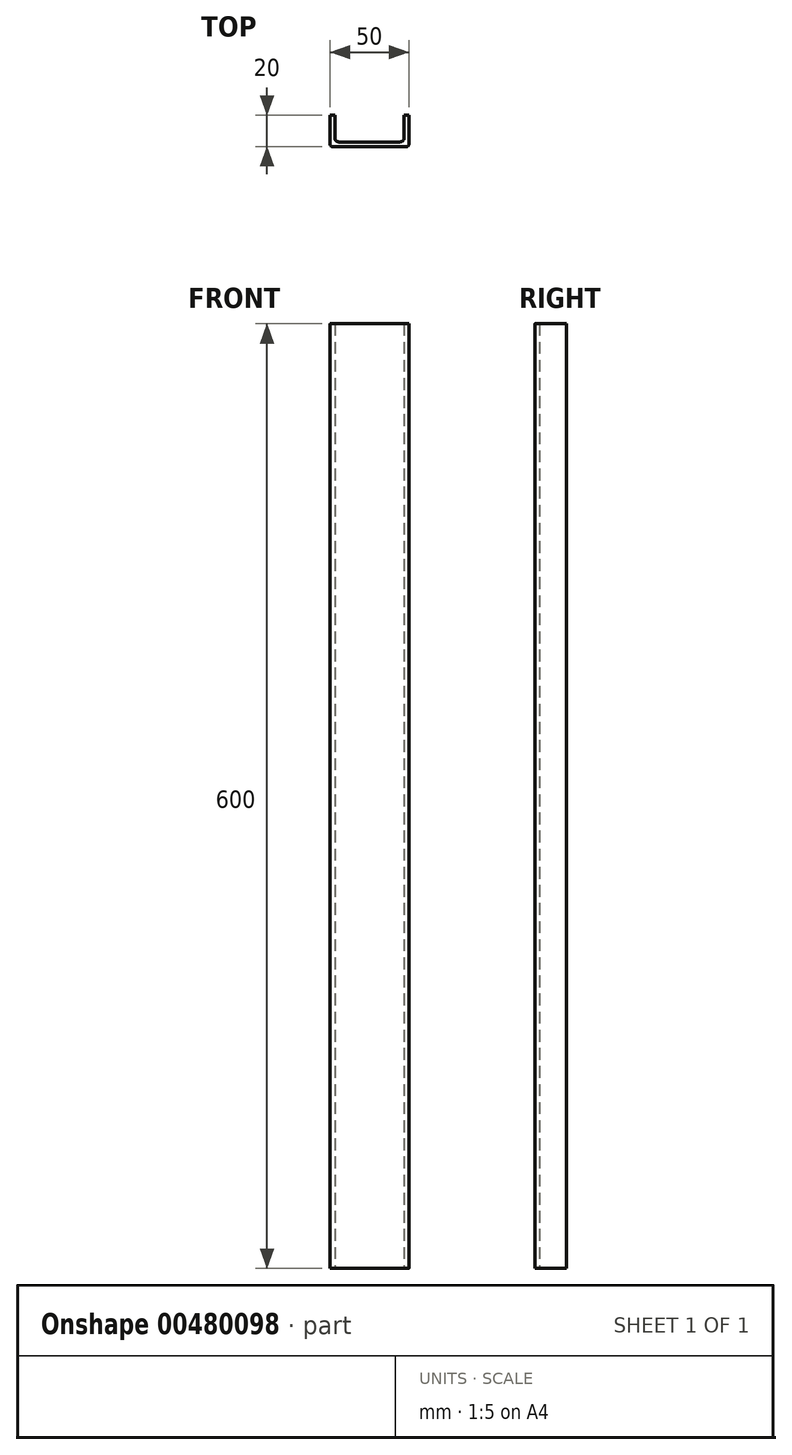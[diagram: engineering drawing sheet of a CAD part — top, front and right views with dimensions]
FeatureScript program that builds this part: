
annotation { "Feature Type Name" : "Feature", "Feature Type Description" : "" }
export const myFeature = defineFeature(function(context is Context, id is Id, definition is map)
    precondition{}
    {
        {
            var Q0;
            Q0=qCreatedBy(makeId("Top.planeOp"),FACE);
            var sketch = newSketch(context, id + "F0", { "sketchPlane" : qUnion([Q0])});
            skArc(sketch, "E0.0.endCap", {"start": v(0, -1.5) * mm, "mid": v(-1.06, -1.06) * mm, "end": v(-1.5, 0) * mm});
            skLineSegment(sketch, "E0.0.left", {"start": v(1.5, 18.5) * mm, "end": v(1.5, 4) * mm});
            skLineSegment(sketch, "E0.0.right", {"start": v(-1.5, 18.5) * mm, "end": v(-1.5, 0) * mm});
            skArc(sketch, "E0.1.startCap", {"start": v(0, -1.5) * mm, "mid": v(-1.06, -1.06) * mm, "end": v(-1.5, 0) * mm});
            skArc(sketch, "E0.1.endCap", {"start": v(48.5, 0) * mm, "mid": v(48.06, -1.06) * mm, "end": v(47, -1.5) * mm});
            skLineSegment(sketch, "E0.1.left", {"start": v(4, 1.5) * mm, "end": v(43, 1.5) * mm});
            skLineSegment(sketch, "E0.1.right", {"start": v(0, -1.5) * mm, "end": v(47, -1.5) * mm});
            skArc(sketch, "E0.2.startCap", {"start": v(48.5, 0) * mm, "mid": v(48.06, -1.06) * mm, "end": v(47, -1.5) * mm});
            skLineSegment(sketch, "E0.2.left", {"start": v(45.5, 4) * mm, "end": v(45.5, 18.5) * mm});
            skLineSegment(sketch, "E0.2.right", {"start": v(48.5, 0) * mm, "end": v(48.5, 18.5) * mm});
            skLineSegment(sketch, "E1", {"start": v(-1.5, 18.5) * mm, "end": v(1.5, 18.5) * mm});
            skLineSegment(sketch, "E2", {"start": v(45.5, 18.5) * mm, "end": v(48.5, 18.5) * mm});
            skPoint(sketch, "E3.orphan", {"position": v(0, 18.5) * mm});
            skPoint(sketch, "E4.end.orphan", {"position": v(47, 18.5) * mm});
            skPoint(sketch, "E5.visualSharp", {"position": v(1.5, 1.5) * mm});
            skArc(sketch, "E5.filletArc", {"start": v(1.5, 4) * mm, "mid": v(2.23, 2.23) * mm, "end": v(4, 1.5) * mm});
            skPoint(sketch, "E6.visualSharp", {"position": v(45.5, 1.5) * mm});
            skArc(sketch, "E6.filletArc", {"start": v(43, 1.5) * mm, "mid": v(44.77, 2.23) * mm, "end": v(45.5, 4) * mm});
            skSolve(sketch);
        }
        {
            var Q0;
            Q0=makeQuery(id+"F0.imprint","IMPRINT",FACE,{"disambiguationData":[TD([[makeQuery(id+"F0.imprint","IMPRINT",EDGE,{"derivedFrom":sQuery(id+"F0.wireOp",EDGE,"E0.0.left")}),-1.0]])]});
            extrude(context, id + "F1", {"entities" : qUnion([Q0]), "depth" : 600 * mm});
        }
    });
